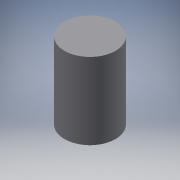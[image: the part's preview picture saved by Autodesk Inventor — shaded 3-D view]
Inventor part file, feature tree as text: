
AUTODESK INVENTOR PART (.ipt)
format: ipt  version: 2019 (Build 230136000, 136)  size: 120,832 bytes
history: native  units: in
note: dims shown in document units (in); Inventor stores cm internally (conversion verified against a paired STEP export)
features: extrude x4, sketch x4
ambient origin geometry x8: Origin, YZ Plane, XZ Plane, XY Plane, X Axis, Y Axis, Z Axis, Center Point
bodies: Solid1 (feature_tree)
feature tree (8):
  extrude  "Extrusion1"  Depth=0.145in TaperAngle=0.0deg
  extrude  "Extrusion2"  Depth=2.25in TaperAngle=0.0deg
  extrude  "Extrusion3"  Depth=0.35in TaperAngle=0.0deg
  extrude  "Extrusion4"  Depth=0.1in
  sketch  "Sketch1"  dims[d0=0.515in d1=0.145in d2=0.0in]
  sketch  "Sketch2"  dims[d3=1.5in d4=2.25in d5=0.0in]
  sketch  "Sketch3"  dims[d6=0.125in d7=0.35in d8=0.0in]
  sketch  "Sketch4"  dims[d9=1.0in d10=0.1in d11=0.1in d12=0.0in]
